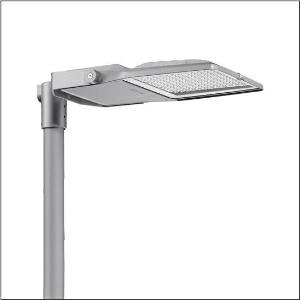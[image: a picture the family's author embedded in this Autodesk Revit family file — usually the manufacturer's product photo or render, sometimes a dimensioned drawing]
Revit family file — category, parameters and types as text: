
# Revit family: floodlight_fl_21_iq_midi___pl33t_5xa7782f4f3a_5715
name_source: partatom
category: Lighting Fixtures
units: mm (PartAtom-declared; Revit-internal decimal feet)

## family parameters
Cut with Voids When Loaded = No
Host = Face
Light Source = No
Part Type = Normal
Room Calculation Point = No
Round Connector Dimension = Use Diameter
Shared = No

## types (1)
- --- (1 x LED, 36900 lm, 270.2 W, 4000K)
    Apparent Load = 270 VA
    CIE Flux Codes = 26 75 99 100 100
    Color Rendering = 70
    Color Temperature = 4000K
    Default Elevation = 1800 mm
    Description = Floodlight FL 21 iQ midi, floodlight, primary light control with lens, of PMMA, primary optical cover: protective disc, of toughened safety glass, transparent, light distribution: PL33T, light emission: direct distribution, installation type: surface-mounted, lamps: LED, High Power LED, rated values: 36.900lm | 270,2W | 136,6lm/W (begin service life); end service life: 36.900lm | 286,6W; at 50% lumin. flux: 18.450lm | 117,7W | 156,8lm/W, colour temperature: 4000K, colour rendering: CRI > 70, light colour: 740, light setting 1 begin service life: 100% | 36.900lm | 270,2W | 136,6lm/W | 4.000K, light setting 1 end service life: 286,6W, further light settings possible, control: optimised constant luminous flux control (CLO 2.0), Desk-Remote (wireless, voltage-free reading and setting of iQ features in the workshop via application-optimized NFC function/RFID function), Smart-Wire, Night-Set, Temp-Guard, Auto-Match, Street-Remote, pre-setting: linear dimming characteristic, with terminal, 6-pole, mains connection: 220..240V, AC, 50/60Hz, luminaire housing, of diecast aluminium, powder-coated, SITECO metallic grey (DB 702S), corrosivity category C5 mid according to DIN EN ISO 12944suitable for swimming poolschlorine-resistant, sealing non-destructively replaceable, please order mast flange separately, mast bracket, of steel, galvanised, powder-coated, SITECO metallic grey (DB 702S), protection rating (complete): IP66, insulation class (complete): insulation class II (safety insulation), certification: CE, ENEC, VDE, protection symbol: D, impact resistance: IK08, permissible operating ambient temperature: -40..+40°C, permissible operating ambient temperature for outdoor applications: -40..+50°C, standard: DIN EN 12944, LABS conformity tested according to VDMA 24364:2018-05, packaging unit: 1 piece

Light Distribution: PL33T
    Height = 76 mm
    Lamp = 1 x LED
    Lamp Light Flux = 36900 lm
    Lamp Power = 270.2 W
    Lamp count = 1
    Length = 657 mm
    Luminous efficacy = 137 lm/W
    Manufacturer = Siteco
    ModVariant = No
    Model = 5XA7782F4F3A
    Mounting Place = Pole
    Mounting Type = Pole annexe
    Number of Poles = 1
    OnlyDefault = Yes
    Power Factor = 1
    Product Name = Floodlight FL 21 iQ midi | PL33T
    Product group = floodlight | pylon annexe
    ProductGroupID = 6201
    Protection Class = Protection class II
    Protection Degree = IP 66
    RLX_Detail_Level = 1
    RLX_Emergency_Light_Flux = 0 lm
    RLX_Emergency_Type = 0
    RLX_Emergency_Type_DB = No
    RlxData = <blob elided: 153757 chars, md5=4cddf5df>
    Socket = socket
    Standby Power = 0 W
    System Light Flux = 36900 lm
    System Power = 270 W
    Type Comments = factory setting: luminous flux: 100 % | dim-lin: 254 | 620 mA
    Type Image = l_1007123.jpg
    URL = http://relux.com
    VarID = @adj_104761
    Voltage = 0 V
    Weight = 0.00 kg
    Width = 442 mm

## geometry (parser evidence)
native form markers: Blend x4, Sweep x12
no freeform markers — native parametric forms only
